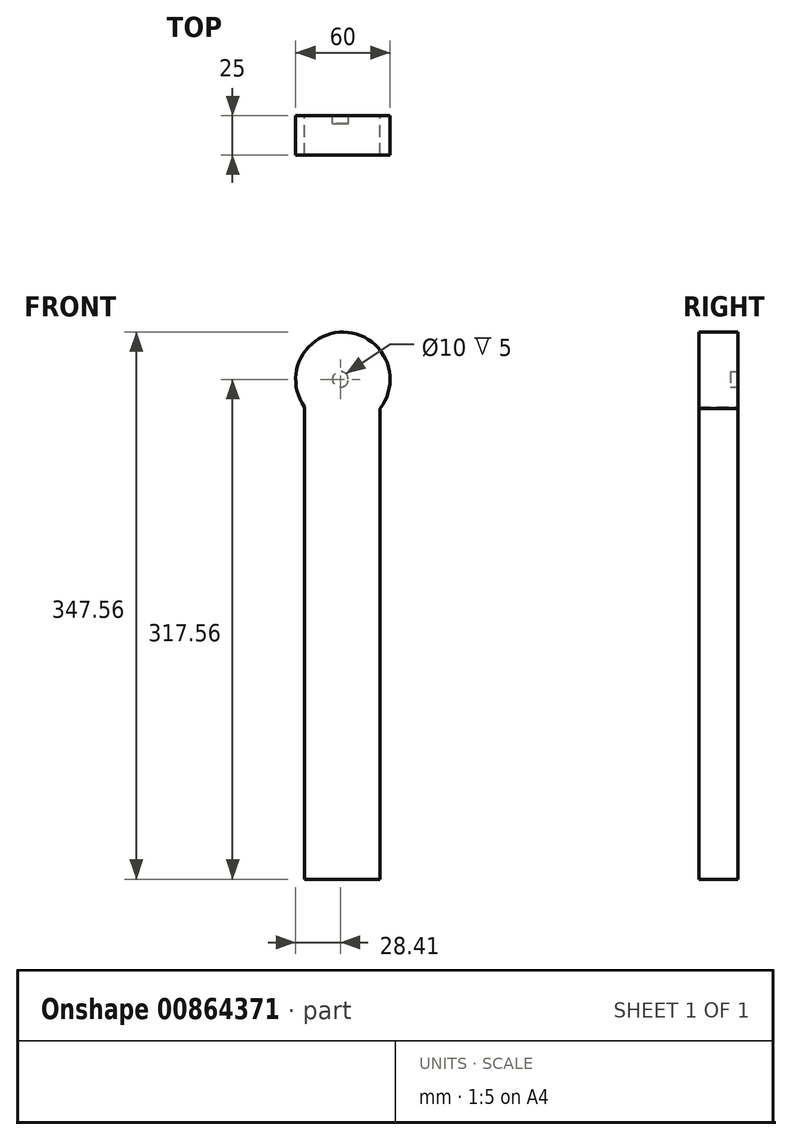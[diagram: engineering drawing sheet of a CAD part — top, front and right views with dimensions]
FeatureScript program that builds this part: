
annotation { "Feature Type Name" : "Feature", "Feature Type Description" : "" }
export const myFeature = defineFeature(function(context is Context, id is Id, definition is map)
    precondition{}
    {
        {
            var Q0;
            Q0=qCreatedBy(makeId("Front.planeOp"),FACE);
            var sketch = newSketch(context, id + "F0", { "sketchPlane" : qUnion([Q0])});
            skCircle(sketch, "E0", {"center": v(1.59, 0) * mm, "radius": 30 * mm});
            skLineSegment(sketch, "E1.bottom", {"start": v(-22.74, -17.56) * mm, "end": v(25.26, -17.56) * mm});
            skLineSegment(sketch, "E1.top", {"start": v(-22.74, -317.56) * mm, "end": v(25.26, -317.56) * mm});
            skLineSegment(sketch, "E1.left", {"start": v(-22.74, -17.56) * mm, "end": v(-22.74, -317.56) * mm});
            skLineSegment(sketch, "E1.right", {"start": v(25.26, -17.56) * mm, "end": v(25.26, -317.56) * mm});
            skSolve(sketch);
        }
        {
            var Q0;
            {var subQ0=sQuery(id+"F0.wireOp",EDGE,"E1.bottom");Q0=makeQuery(id+"F0.imprint","IMPRINT",FACE,{"disambiguationData":[TD([[makeQuery(id+"F0.imprint","IMPRINT",EDGE,{"derivedFrom":subQ0}),1.0]])]});}
            var Q1;
            {var subQ0=sQuery(id+"F0.wireOp",EDGE,"E1.bottom");Q1=makeQuery(id+"F0.imprint","IMPRINT",FACE,{"disambiguationData":[TD([[makeQuery(id+"F0.imprint","IMPRINT",EDGE,{"derivedFrom":subQ0}),-1.0]])]});}
            var Q2;
            {var subQ4=sQuery(id+"F0.wireOp",EDGE,"E1.top");Q2=makeQuery(id+"F0.imprint","IMPRINT",FACE,{"disambiguationData":[TD([[makeQuery(id+"F0.imprint","IMPRINT",EDGE,{"derivedFrom":subQ4}),1.0]])]});}
            extrude(context, id + "F1", {"entities" : qUnion([Q0, Q1, Q2]), "depth" : 25 * mm, "offsetDistance" : 25 * mm});
        }
        {
            var Q0;
            Q0=makeQuery(id+"F1.opExtrude","CAP_FACE",FACE,{"disambiguationData":[OSD([sQuery(id+"F0.wireOp",EDGE,"E0"),sQuery(id+"F0.wireOp",EDGE,"E1.top"),sQuery(id+"F0.wireOp",EDGE,"E1.left"),sQuery(id+"F0.wireOp",EDGE,"E1.right")])],"isStart":true});
            var sketch = newSketch(context, id + "F2", { "sketchPlane" : qUnion([Q0])});
            skCircle(sketch, "E2", {"center": v(0, 0) * mm, "radius": 5 * mm});
            skSolve(sketch);
        }
        {
            var Q0;
            Q0=makeQuery(id+"F2.imprint","IMPRINT",FACE,{"disambiguationData":[TD([[makeQuery(id+"F2.imprint","IMPRINT",EDGE,{"derivedFrom":sQuery(id+"F2.wireOp",EDGE,"E2")}),1.0]])]});
            extrude(context, id + "F3", {"entities" : qUnion([Q0]), "operationType" : NewBodyOperationType.REMOVE, "oppositeDirection" : true, "depth" : 5 * mm, "offsetDistance" : 25 * mm});
        }
    });
